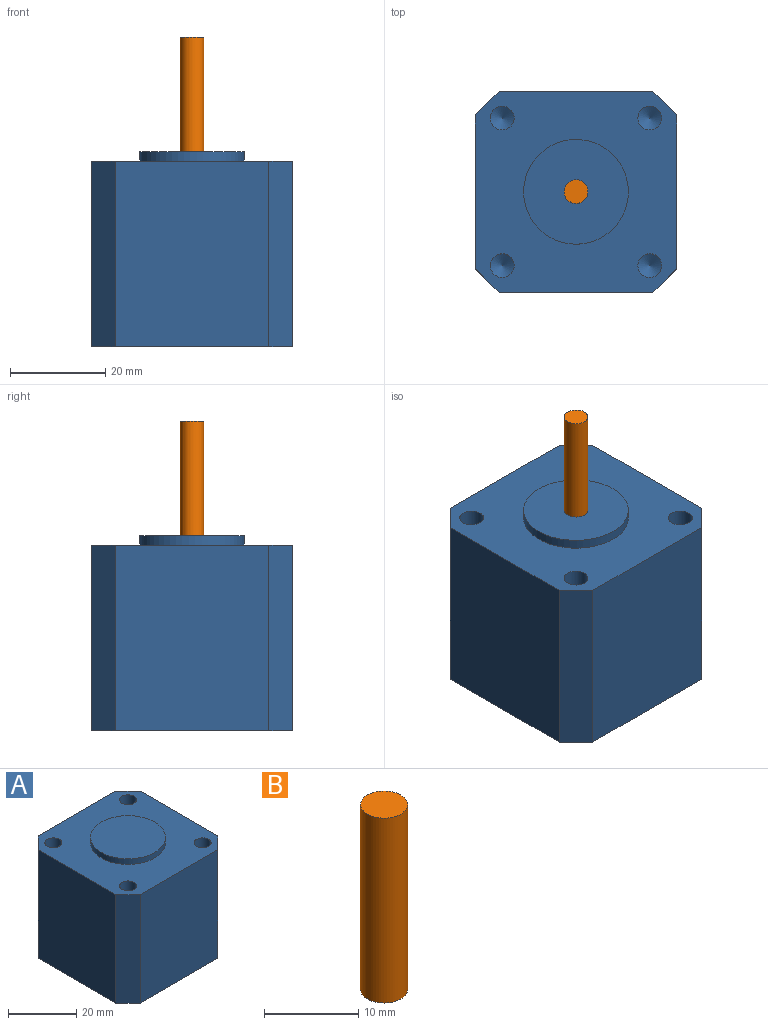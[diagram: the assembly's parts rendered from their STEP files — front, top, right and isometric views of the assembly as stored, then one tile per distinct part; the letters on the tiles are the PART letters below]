
ASSEMBLY  parts=2 mates=1
PART A: 20 faces, bbox 42.3x42.3x41 mm
  f0: plane 39x32.3mm, normal (-1,0,0), area 1259.7mm2, adj f4,f5,f18,f19
  f1: plane 39x32.3mm, normal (0,-1,0), area 1259.7mm2, adj f4,f5,f17,f18
  f2: plane 39x32.3mm, normal (1,0,0), area 1259.7mm2, adj f4,f5,f16,f17
  f3: plane 39x32.3mm, normal (0,1,0), area 1259.7mm2, adj f4,f5,f16,f19
  f4: plane 42.3x42.3mm, normal (0,0,1), area 1280.6mm2, adj f0,f1,f2,f3,f6,f8,f10,f12
  f5: plane 42.3x42.3mm, normal (0,0,-1), area 1739.3mm2, adj f0,f1,f2,f3,f16,f17,f18,f19
  f6: cylinder r=11mm len=22mm, axis (0,0,-1), area 138.2mm2, adj f4,f7
  f7: plane 22x22mm, normal (0,0,1), area 380.1mm2, adj f6
  f8: cylinder r=2.5mm len=20mm, axis (0,0,1), area 314.2mm2, adj f4,f9
  f9: cone r=0mm half-angle=59deg, axis (0,0,1), area 22.9mm2, adj f8
  f10: cylinder r=2.5mm len=20mm, axis (0,0,1), area 314.2mm2, adj f4,f11
  f11: cone r=0mm half-angle=59deg, axis (0,0,1), area 22.9mm2, adj f10
  f12: cylinder r=2.5mm len=20mm, axis (0,0,1), area 314.2mm2, adj f4,f13
  f13: cone r=0mm half-angle=59deg, axis (0,0,1), area 22.9mm2, adj f12
  f14: cylinder r=2.5mm len=20mm, axis (0,0,1), area 314.2mm2, adj f4,f15
  f15: cone r=0mm half-angle=59deg, axis (0,0,1), area 22.9mm2, adj f14
  f16: plane 39x5mm, normal (0.71,0.71,0), area 275.8mm2, adj f2,f3,f4,f5
  f17: plane 39x5mm, normal (0.71,-0.71,0), area 275.8mm2, adj f1,f2,f4,f5
  f18: plane 39x5mm, normal (-0.71,-0.71,0), area 275.8mm2, adj f0,f1,f4,f5
  f19: plane 39x5mm, normal (-0.71,0.71,0), area 275.8mm2, adj f0,f3,f4,f5
PART B: 3 faces, bbox 5x5x24 mm
  f0: cylinder r=2.5mm len=24mm, axis (0,0,-1), area 377mm2, adj f1,f2
  f1: plane 5x5mm, normal (0,0,1), area 19.6mm2, adj f0
  f2: plane 5x5mm, normal (0,0,-1), area 19.6mm2, adj f0
PLACE A at identity
PLACE B at identity
MATE revolute B.f0 <-> A.f6  axis (0,0,-1) through (21.15,21.15,41)mm
